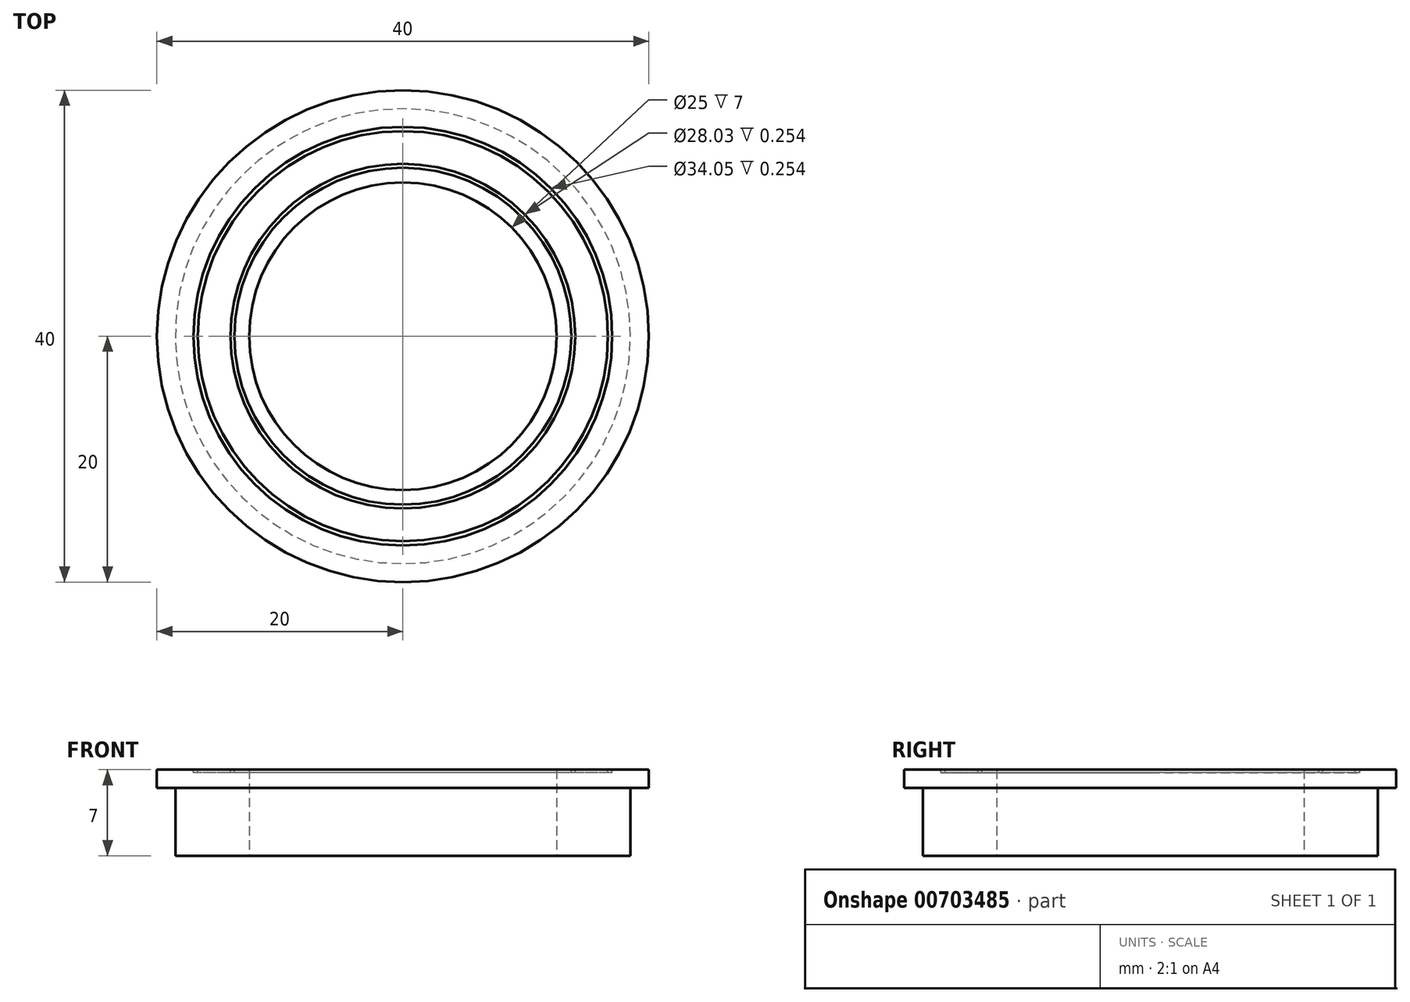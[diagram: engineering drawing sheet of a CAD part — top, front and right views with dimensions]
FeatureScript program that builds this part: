
annotation { "Feature Type Name" : "Feature", "Feature Type Description" : "" }
export const myFeature = defineFeature(function(context is Context, id is Id, definition is map)
    precondition{}
    {
        {
            var Q0;
            Q0=qCreatedBy(makeId("Top.planeOp"),FACE);
            var sketch = newSketch(context, id + "F0", { "sketchPlane" : qUnion([Q0])});
            skCircle(sketch, "E0", {"center": v(0, 0) * mm, "radius": 18.5 * mm});
            skCircle(sketch, "E1", {"center": v(0, 0) * mm, "radius": 12.5 * mm});
            skSolve(sketch);
        }
        {
            var Q0;
            Q0=makeQuery(id+"F0.imprint","IMPRINT",FACE,{"disambiguationData":[TD([[makeQuery(id+"F0.imprint","IMPRINT",EDGE,{"derivedFrom":sQuery(id+"F0.wireOp",EDGE,"E0")}),1.0]])]});
            extrude(context, id + "F1", {"entities" : qUnion([Q0]), "depth" : 7 * mm});
        }
        {
            var Q0;
            Q0=makeQuery(id+"F1.opExtrude","CAP_FACE",FACE,{"disambiguationData":[OSD([sQuery(id+"F0.wireOp",EDGE,"E0"),sQuery(id+"F0.wireOp",EDGE,"E1")])],"isStart":false});
            var sketch = newSketch(context, id + "F2", { "sketchPlane" : qUnion([Q0])});
            skCircle(sketch, "E2", {"center": v(0, 0) * mm, "radius": 13.7 * mm});
            skCircle(sketch, "E3", {"center": v(0, 0) * mm, "radius": 14.02 * mm});
            skSolve(sketch);
        }
        {
            var Q0;
            Q0=qSketchRegion(id+"F2",true);
            extrude(context, id + "F3", {"entities" : qUnion([Q0]), "operationType" : NewBodyOperationType.REMOVE, "oppositeDirection" : true, "depth" : 0.25 * mm});
        }
        {
            var Q0;
            {var subQ0=sQuery(id+"F0.wireOp",EDGE,"E0");Q0=makeQuery(id+"F3.boolean.opBoolean","SPLIT",FACE,{"disambiguationData":[TD([makeQuery(id+"F1.opExtrude","SWEPT_FACE",FACE,{"disambiguationData":[OSD([subQ0])]})])],"derivedFrom":makeQuery(id+"F1.opExtrude","CAP_FACE",FACE,{"disambiguationData":[OSD([subQ0,sQuery(id+"F0.wireOp",EDGE,"E1")])],"isStart":false})});}
            var sketch = newSketch(context, id + "F4", { "sketchPlane" : qUnion([Q0])});
            skCircle(sketch, "E4", {"center": v(0, 0) * mm, "radius": 17.02 * mm});
            skCircle(sketch, "E5", {"center": v(0, 0) * mm, "radius": 16.67 * mm});
            skSolve(sketch);
        }
        {
            var Q0;
            Q0=qSketchRegion(id+"F4",true);
            extrude(context, id + "F5", {"entities" : qUnion([Q0]), "operationType" : NewBodyOperationType.REMOVE, "oppositeDirection" : true, "depth" : 0.25 * mm});
        }
        {
            var Q0;
            {var subQ0=sQuery(id+"F0.wireOp",EDGE,"E0");var subQ1=makeQuery(id+"F1.opExtrude","SWEPT_FACE",FACE,{"disambiguationData":[OSD([subQ0])]});Q0=makeQuery(id+"F5.boolean.opBoolean","SPLIT",FACE,{"disambiguationData":[TD([subQ1])],"derivedFrom":makeQuery(id+"F3.boolean.opBoolean","SPLIT",FACE,{"disambiguationData":[TD([subQ1])],"derivedFrom":makeQuery(id+"F1.opExtrude","CAP_FACE",FACE,{"disambiguationData":[OSD([subQ0,sQuery(id+"F0.wireOp",EDGE,"E1")])],"isStart":false})})});}
            var sketch = newSketch(context, id + "F6", { "sketchPlane" : qUnion([Q0])});
            skCircle(sketch, "E6", {"center": v(0, 0) * mm, "radius": 20 * mm});
            skCircle(sketch, "E7", {"center": v(0, 0) * mm, "radius": 18.5 * mm});
            skSolve(sketch);
        }
        {
            var Q0;
            Q0=qSketchRegion(id+"F6",true);
            extrude(context, id + "F7", {"entities" : qUnion([Q0]), "operationType" : NewBodyOperationType.ADD, "depth" : -1.5 * mm, "offsetDistance" : 25.4 * mm});
        }
    });
